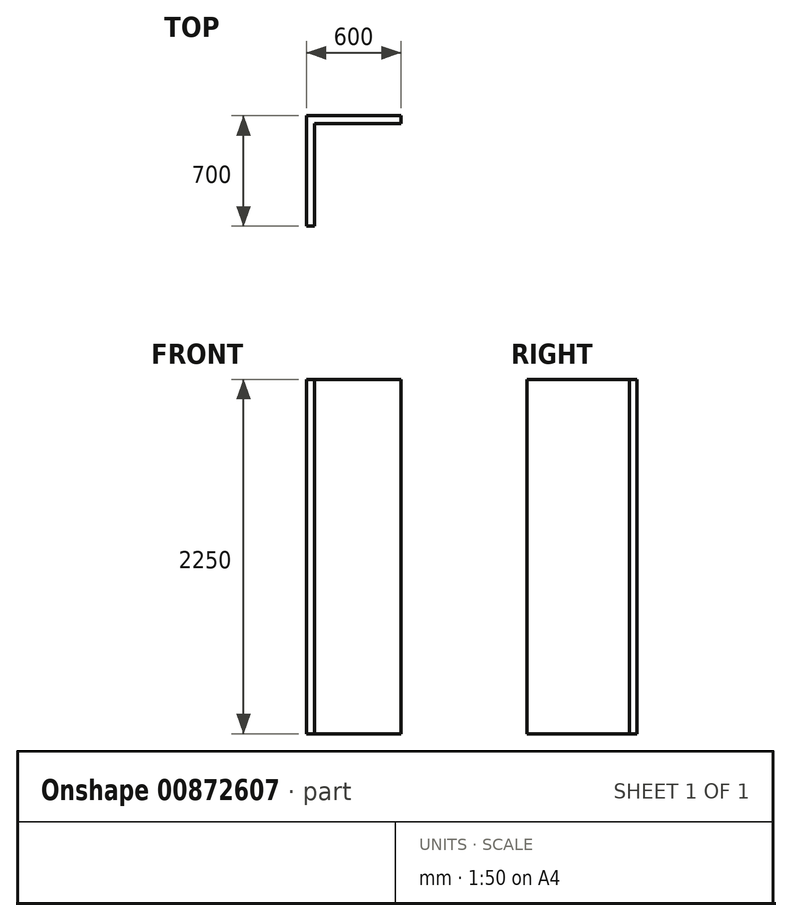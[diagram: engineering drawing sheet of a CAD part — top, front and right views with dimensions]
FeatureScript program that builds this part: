
annotation { "Feature Type Name" : "Feature", "Feature Type Description" : "" }
export const myFeature = defineFeature(function(context is Context, id is Id, definition is map)
    precondition{}
    {
        {
            var Q0;
            Q0=qCreatedBy(makeId("Top.planeOp"),FACE);
            var sketch = newSketch(context, id + "F0", { "sketchPlane" : qUnion([Q0])});
            skLineSegment(sketch, "E0", {"start": v(0, 0) * mm, "end": v(0, -650) * mm});
            skLineSegment(sketch, "E1", {"start": v(0, -650) * mm, "end": v(-50, -650) * mm});
            skLineSegment(sketch, "E2", {"start": v(-50, -650) * mm, "end": v(-50, 50) * mm});
            skLineSegment(sketch, "E3", {"start": v(-50, 50) * mm, "end": v(550, 50) * mm});
            skLineSegment(sketch, "E4", {"start": v(550, 50) * mm, "end": v(550, 0) * mm});
            skLineSegment(sketch, "E5", {"start": v(550, 0) * mm, "end": v(0, 0) * mm});
            skSolve(sketch);
        }
        {
            var Q0;
            Q0 = qSketchRegion(id + "F0", true);
            extrude(context, id + "F1", {"entities" : qUnion([Q0]), "depth" : 2250 * mm, "offsetDistance" : 25 * mm});
        }
    });
